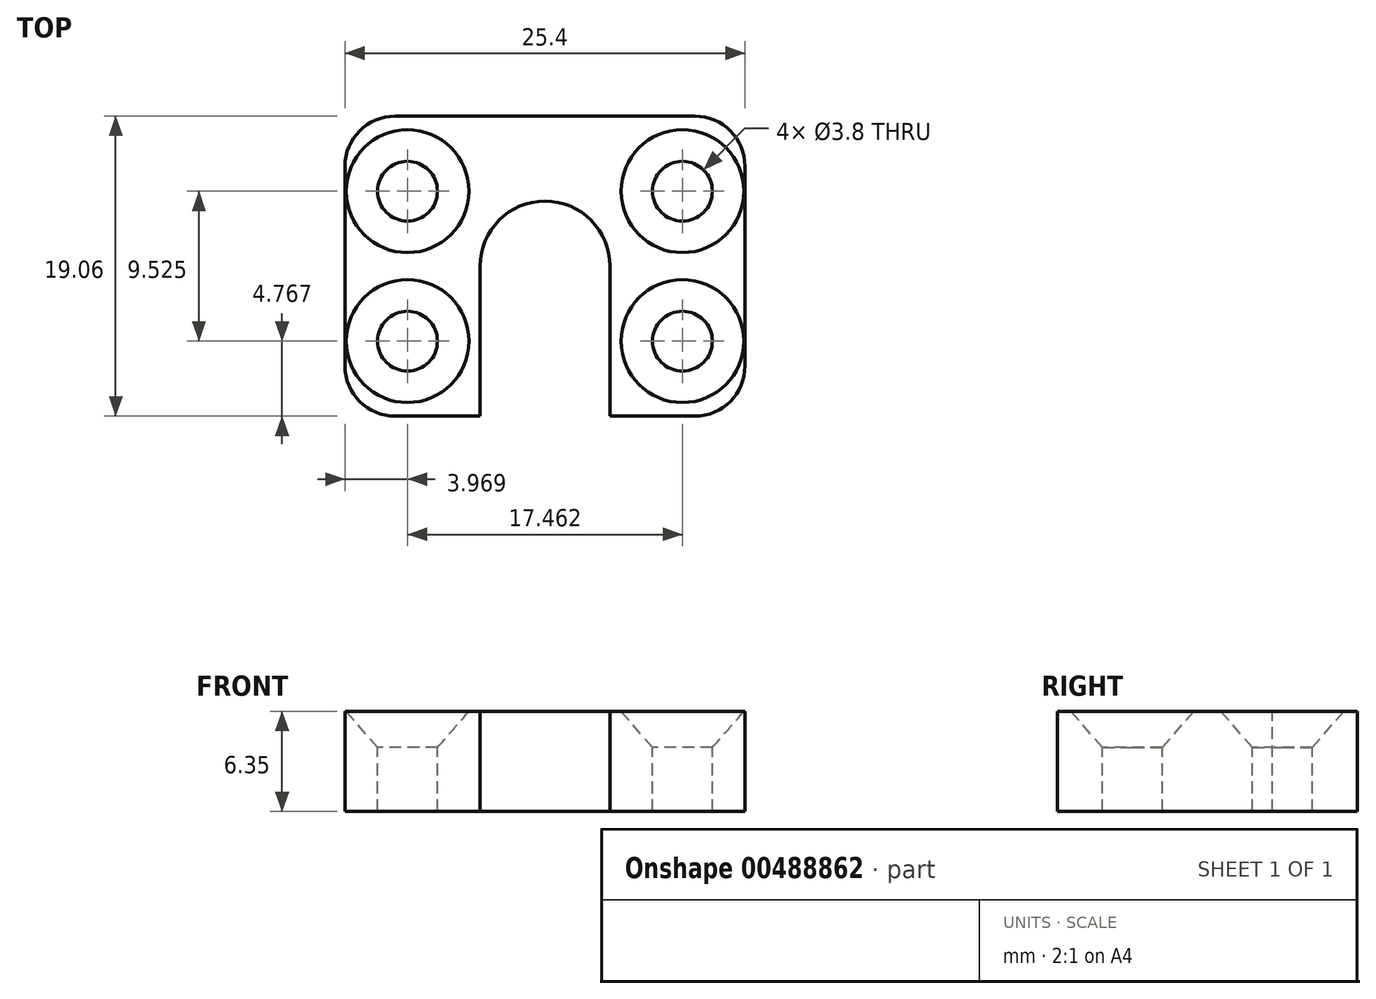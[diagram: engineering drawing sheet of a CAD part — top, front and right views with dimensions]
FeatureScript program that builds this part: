
annotation { "Feature Type Name" : "Feature", "Feature Type Description" : "" }
export const myFeature = defineFeature(function(context is Context, id is Id, definition is map)
    precondition{}
    {
        {
            var Q0;
            Q0=qCreatedBy(makeId("Top.planeOp"),FACE);
            var sketch = newSketch(context, id + "F0", { "sketchPlane" : qUnion([Q0])});
            skLineSegment(sketch, "E0.bottom", {"start": v(12.7, 9.52) * mm, "end": v(-12.7, 9.52) * mm});
            skLineSegment(sketch, "E0.top", {"start": v(12.7, -9.53) * mm, "end": v(-12.7, -9.53) * mm});
            skLineSegment(sketch, "E0.left", {"start": v(12.7, 9.52) * mm, "end": v(12.7, -9.53) * mm});
            skLineSegment(sketch, "E0.right", {"start": v(-12.7, 9.53) * mm, "end": v(-12.7, -9.53) * mm});
            skPoint(sketch, "E0.middle", {"position": v(0, 0) * mm});
            skSolve(sketch);
        }
        {
            var Q0;
            Q0 = qSketchRegion(id + "F0", true);
            extrude(context, id + "F1", {"entities" : qUnion([Q0]), "depth" : 6.35 * mm});
        }
        {
            var Q0;
            Q0=makeQuery(id+"F1.opExtrude","CAP_FACE",FACE,{"disambiguationData":[OSD([sQuery(id+"F0.wireOp",EDGE,"E0.bottom"),sQuery(id+"F0.wireOp",EDGE,"E0.top"),sQuery(id+"F0.wireOp",EDGE,"E0.left"),sQuery(id+"F0.wireOp",EDGE,"E0.right")])],"isStart":false});
            var sketch = newSketch(context, id + "F2", { "sketchPlane" : qUnion([Q0])});
            skLineSegment(sketch, "E1", {"start": v(0, -9.52) * mm, "end": v(0, 9.52) * mm, "construction": true});
            skArc(sketch, "E2", {"start": v(4.13, 0) * mm, "mid": v(0, 4.13) * mm, "end": v(-4.13, 0) * mm});
            skLineSegment(sketch, "E3", {"start": v(-4.13, 0) * mm, "end": v(-4.13, -9.53) * mm});
            skLineSegment(sketch, "E4", {"start": v(-4.13, -9.53) * mm, "end": v(4.13, -9.53) * mm});
            skLineSegment(sketch, "E5", {"start": v(4.13, -9.53) * mm, "end": v(4.13, 0) * mm});
            skSolve(sketch);
        }
        {
            var Q0;
            Q0 = qSketchRegion(id + "F2", true);
            extrude(context, id + "F3", {"entities" : qUnion([Q0]), "operationType" : NewBodyOperationType.REMOVE, "endBound" : BoundingType.THROUGH_ALL, "oppositeDirection" : true, "depth" : 25.4 * mm});
        }
        {
            var Q0;
            Q0=makeQuery(id+"F1.opExtrude","CAP_FACE",FACE,{"disambiguationData":[OSD([sQuery(id+"F0.wireOp",EDGE,"E0.bottom"),sQuery(id+"F0.wireOp",EDGE,"E0.top"),sQuery(id+"F0.wireOp",EDGE,"E0.left"),sQuery(id+"F0.wireOp",EDGE,"E0.right")])],"isStart":false});
            var sketch = newSketch(context, id + "F4", { "sketchPlane" : qUnion([Q0])});
            skPoint(sketch, "E6", {"position": v(-8.73, 4.76) * mm});
            skPoint(sketch, "E7", {"position": v(-8.73, -4.76) * mm});
            skPoint(sketch, "E8", {"position": v(8.73, -4.76) * mm});
            skPoint(sketch, "E9", {"position": v(8.73, 4.76) * mm});
            skLineSegment(sketch, "E10", {"start": v(-8.73, 4.76) * mm, "end": v(-8.73, -4.76) * mm, "construction": true});
            skLineSegment(sketch, "E11", {"start": v(-8.73, -4.76) * mm, "end": v(8.73, -4.76) * mm, "construction": true});
            skLineSegment(sketch, "E12", {"start": v(0, 0) * mm, "end": v(0, -4.76) * mm, "construction": true});
            skLineSegment(sketch, "E13", {"start": v(-8.73, 0) * mm, "end": v(0, 0) * mm, "construction": true});
            skSolve(sketch);
        }
        {
            var Q0;
            Q0=sQuery(id+"F4.wireOp",VERTEX,"E6");
            var Q1;
            Q1=sQuery(id+"F4.wireOp",VERTEX,"E9");
            var Q2;
            Q2=sQuery(id+"F4.wireOp",VERTEX,"E8");
            var Q3;
            Q3=sQuery(id+"F4.wireOp",VERTEX,"E7");
            var Q4;
            Q4=makeQuery(id+"F1.opExtrude","SWEPT_BODY",BODY,{"disambiguationData":[OSD([sQuery(id+"F0.wireOp",EDGE,"E0.bottom"),sQuery(id+"F0.wireOp",EDGE,"E0.top"),sQuery(id+"F0.wireOp",EDGE,"E0.left"),sQuery(id+"F0.wireOp",EDGE,"E0.right")])]});
            hole(context, id + "F5", {"style" : HoleStyle.C_SINK, "endStyle" : HoleEndStyle.THROUGH, "standardTappedOrClearance" : lookupTablePath({ "standard" : "ANSI", "fit" : "Normal (ASME)", "size" : "#6", "type" : "Clearance" }), "standardBlindInLast" : lookupTablePath({ "fit" : "Free", "standard" : "ANSI", "size" : "#6", "type" : "Clearance" }), "holeDiameter" : 3.8 * mm, "cSinkDiameter" : 7.8 * mm, "cSinkAngle" : 82 * degree, "isTappedThrough" : true, "tappedDepth" : 12.7 * mm, "tapClearance" : 3, "locations" : qUnion([Q0, Q1, Q2, Q3]), "scope" : qUnion([Q4])});
        }
        {
            var Q0;
            Q0=makeQuery(id+"F1.opExtrude","SWEPT_EDGE",EDGE,{"disambiguationData":[OSD([sQuery(id+"F0.wireOp",EDGE,"E0.bottom"),sQuery(id+"F0.wireOp",EDGE,"E0.right")])]});
            var Q1;
            Q1=makeQuery(id+"F1.opExtrude","SWEPT_EDGE",EDGE,{"disambiguationData":[OSD([sQuery(id+"F0.wireOp",EDGE,"E0.top"),sQuery(id+"F0.wireOp",EDGE,"E0.right")])]});
            var Q2;
            Q2=makeQuery(id+"F1.opExtrude","SWEPT_EDGE",EDGE,{"disambiguationData":[OSD([sQuery(id+"F0.wireOp",EDGE,"E0.top"),sQuery(id+"F0.wireOp",EDGE,"E0.left")])]});
            var Q3;
            Q3=makeQuery(id+"F1.opExtrude","SWEPT_EDGE",EDGE,{"disambiguationData":[OSD([sQuery(id+"F0.wireOp",EDGE,"E0.bottom"),sQuery(id+"F0.wireOp",EDGE,"E0.left")])]});
            fillet(context, id + "F6", {"entities" : qUnion([Q0, Q1, Q2, Q3]), "radius" : 3.17 * mm, "tangentPropagation" : true, "allowEdgeOverflow" : false});
        }
    });
